# Revit family: 94020-203
name_source: partatom
category: Modelos genéricos
revit_build: Autodesk Revit 2016 (Build: 20150220_1215(x64)
units: mm (PartAtom-declared; Revit-internal decimal feet)

## family parameters
Com base no plano de trabalho = Não
Compartilhado = Não
Corte com vazios quando carregados = Não
Cota do conector redondo = Utilizar diâmetro
Pode hospedar o vergalhão = Não
Ponto de cálculo do ambiente = Não
Sempre na vertical = Sim
Tipo de parte = Normal

## types (1)
- 94020-203 CUBA RETANGULAR 40 X 34
    Comentários de tipos = Ler Manual de Instalação
    Código de montagem = 94020-203 CUBA RETANGULAR 40 X 34
    Dados de instalação = http://www.tramontina.com
    Descrição = 94020-203 CUBA RETANGULAR 40 X 34
    Desenvolvedor = Factory Cursos & Desenvolvimento
    Diametro = 40  [stored 0.131234 ft]
    Dimensões (mm) = 430X370
    Fabricante = Tramontina
    Modelo = 94020-203
    Site do desenvolvedor = www.factorycursos.com.br
    Tipo de imagem = 94020203_5.jpg
    URL = www.tramontina.com.br

note: [stored X ft] marks values corroborated as IEEE doubles in the binary element streams (Revit-internal decimal feet)
